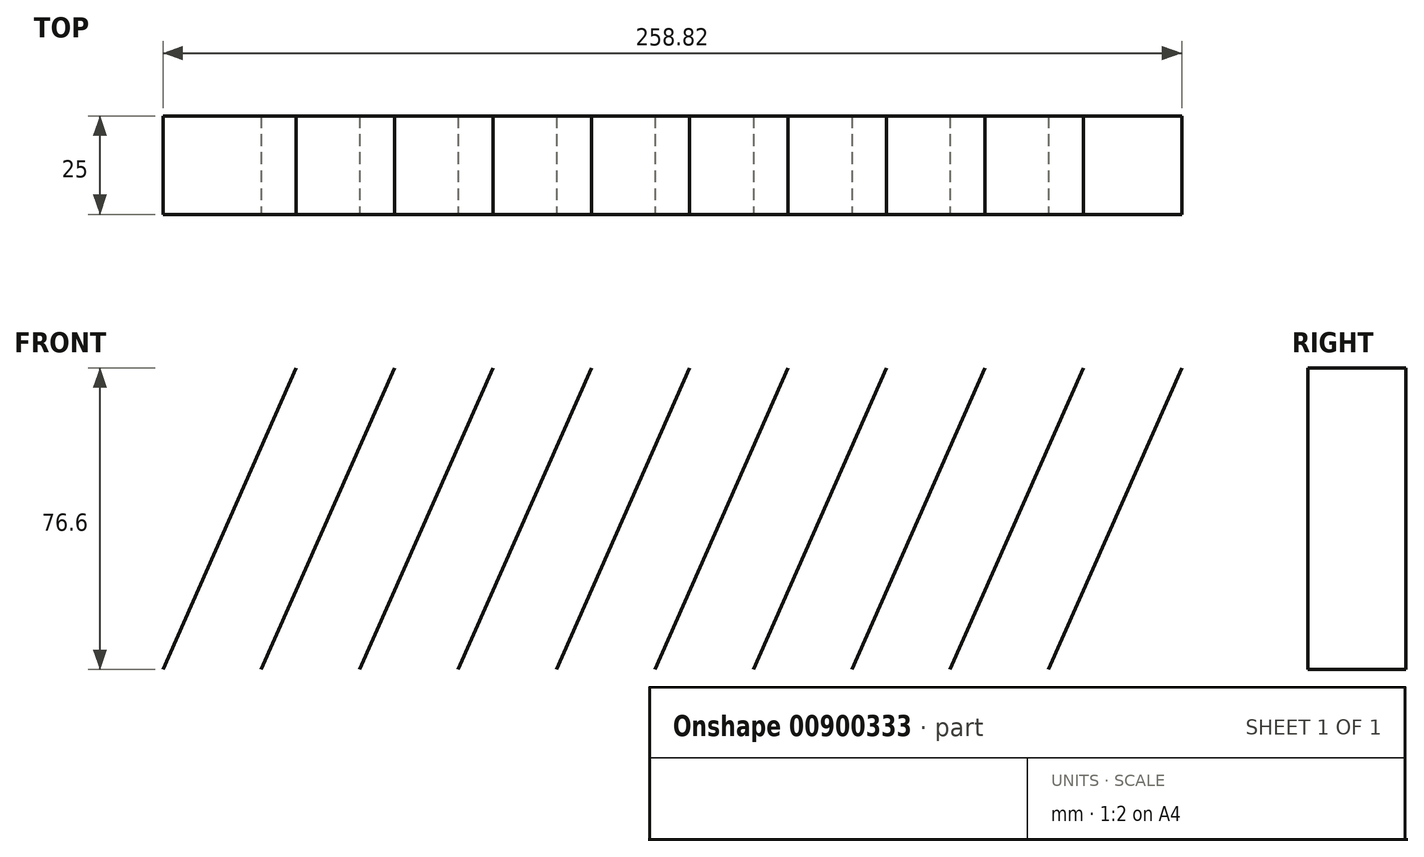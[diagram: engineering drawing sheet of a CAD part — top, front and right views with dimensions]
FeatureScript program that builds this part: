
annotation { "Feature Type Name" : "Feature", "Feature Type Description" : "" }
export const myFeature = defineFeature(function(context is Context, id is Id, definition is map)
    precondition{}
    {
        {
            var Q0;
            Q0=qCreatedBy(makeId("Front.planeOp"),FACE);
            var sketch = newSketch(context, id + "F0", { "sketchPlane" : qUnion([Q0])});
            skLineSegment(sketch, "E0", {"start": v(-180.09, -6.8) * mm, "end": v(-146.27, 69.8) * mm});
            skLineSegment(sketch, "E1.1.0.0", {"start": v(-155.09, -6.8) * mm, "end": v(-121.27, 69.8) * mm});
            skLineSegment(sketch, "E1.2.0.0", {"start": v(-130.09, -6.8) * mm, "end": v(-96.27, 69.8) * mm});
            skLineSegment(sketch, "E1.3.0.0", {"start": v(-105.09, -6.8) * mm, "end": v(-71.27, 69.8) * mm});
            skLineSegment(sketch, "E1.4.0.0", {"start": v(-80.09, -6.8) * mm, "end": v(-46.27, 69.8) * mm});
            skLineSegment(sketch, "E1.5.0.0", {"start": v(-55.09, -6.8) * mm, "end": v(-21.27, 69.8) * mm});
            skLineSegment(sketch, "E1.6.0.0", {"start": v(-30.09, -6.8) * mm, "end": v(3.73, 69.8) * mm});
            skLineSegment(sketch, "E1.7.0.0", {"start": v(-5.09, -6.8) * mm, "end": v(28.73, 69.8) * mm});
            skLineSegment(sketch, "E1.8.0.0", {"start": v(19.91, -6.8) * mm, "end": v(53.73, 69.8) * mm});
            skLineSegment(sketch, "E1.9.0.0", {"start": v(44.91, -6.8) * mm, "end": v(78.73, 69.8) * mm});
            skLineSegment(sketch, "E1.direction1", {"start": v(-180.09, -6.8) * mm, "end": v(-155.09, -6.8) * mm, "construction": true});
            skSolve(sketch);
        }
        {
            var Q0;
            Q0=sQuery(id+"F0.wireOp",EDGE,"E1.2.0.0");
            var Q1;
            Q1=sQuery(id+"F0.wireOp",EDGE,"E1.9.0.0");
            var Q2;
            Q2=sQuery(id+"F0.wireOp",EDGE,"E1.3.0.0");
            var Q3;
            Q3=sQuery(id+"F0.wireOp",EDGE,"E1.6.0.0");
            var Q4;
            Q4=sQuery(id+"F0.wireOp",EDGE,"E1.4.0.0");
            var Q5;
            Q5=sQuery(id+"F0.wireOp",EDGE,"E1.7.0.0");
            var Q6;
            Q6=sQuery(id+"F0.wireOp",EDGE,"E1.1.0.0");
            var Q7;
            Q7=sQuery(id+"F0.wireOp",EDGE,"E1.5.0.0");
            var Q8;
            Q8=sQuery(id+"F0.wireOp",EDGE,"E1.8.0.0");
            var Q9;
            Q9=sQuery(id+"F0.wireOp",EDGE,"E0");
            extrude(context, id + "F1", {"bodyType" : ToolBodyType.SURFACE, "surfaceEntities" : qUnion([Q0, Q1, Q2, Q3, Q4, Q5, Q6, Q7, Q8, Q9]), "depth" : 25 * mm, "offsetDistance" : 25 * mm});
        }
    });
